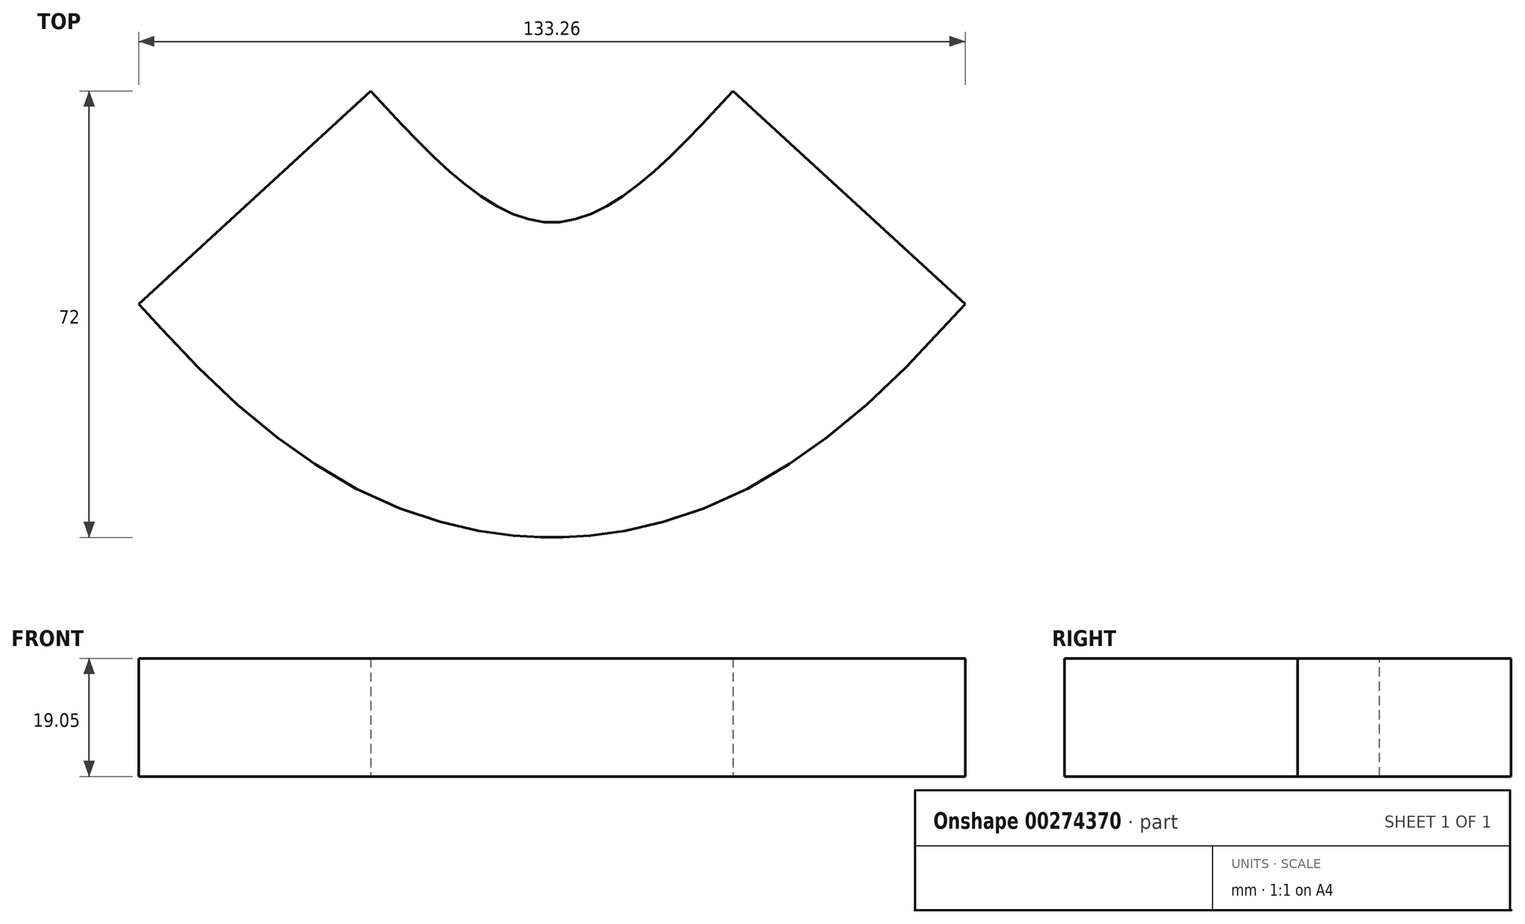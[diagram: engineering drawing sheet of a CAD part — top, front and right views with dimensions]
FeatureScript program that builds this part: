
annotation { "Feature Type Name" : "Feature", "Feature Type Description" : "" }
export const myFeature = defineFeature(function(context is Context, id is Id, definition is map)
    precondition{}
    {
        {
            var Q0;
            Q0=qCreatedBy(makeId("Top.planeOp"),FACE);
            var sketch = newSketch(context, id + "F0", { "sketchPlane" : qUnion([Q0])});
            skFitSpline(sketch, "E0", {"points": [v(-29.21, 50.2) * mm, v(0, 28.99) * mm, v(29.21, 50.2) * mm], "startDerivative": vector(58.42, -63.61) * mm, "endDerivative": vector(58.42, 63.61) * mm});
            skFitSpline(sketch, "E1.0", {"points": [v(-66.63, 15.83) * mm, v(-65.4, 14.5) * mm, v(-62.8, 11.66) * mm, v(-58.31, 6.93) * mm, v(-53.13, 1.79) * mm, v(-48, -2.78) * mm, v(-43.19, -6.55) * mm, v(-39.13, -9.43) * mm, v(-34.53, -12.3) * mm, v(-29.28, -15.08) * mm, v(-24.26, -17.24) * mm, v(-19.8, -18.77) * mm, v(-16.25, -19.78) * mm, v(-12.48, -20.64) * mm, v(-9.16, -21.18) * mm, v(-6.42, -21.5) * mm, v(-4.31, -21.68) * mm, v(-2.53, -21.77) * mm, v(-1.1, -21.8) * mm, v(0, -21.81) * mm, v(1.1, -21.8) * mm, v(2.53, -21.77) * mm, v(4.31, -21.68) * mm, v(6.42, -21.5) * mm, v(9.16, -21.18) * mm, v(12.48, -20.64) * mm, v(16.25, -19.78) * mm, v(19.8, -18.77) * mm, v(24.26, -17.24) * mm, v(29.28, -15.08) * mm, v(34.53, -12.3) * mm, v(39.13, -9.43) * mm, v(43.19, -6.55) * mm, v(48, -2.78) * mm, v(53.13, 1.79) * mm, v(58.31, 6.93) * mm, v(62.8, 11.66) * mm, v(65.4, 14.5) * mm, v(66.63, 15.83) * mm]});
            skLineSegment(sketch, "E2", {"start": v(-29.21, 50.2) * mm, "end": v(-66.63, 15.83) * mm});
            skLineSegment(sketch, "E3", {"start": v(29.21, 50.2) * mm, "end": v(66.63, 15.83) * mm});
            skSolve(sketch);
        }
        {
            var Q0;
            Q0 = qSketchRegion(id + "F0", true);
            extrude(context, id + "F1", {"entities" : qUnion([Q0]), "depth" : 19.05 * mm});
        }
    });
